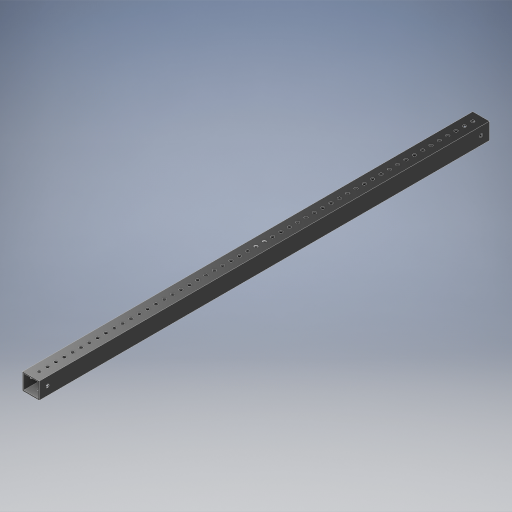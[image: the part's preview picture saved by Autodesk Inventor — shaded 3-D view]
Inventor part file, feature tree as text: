
AUTODESK INVENTOR PART (.ipt)
format: ipt  version: 2024.2 (Build 282272000, 272)  size: 855,040 bytes
history: native  units: in
note: dims shown in document units (in); Inventor stores cm internally (conversion verified against a paired STEP export)
features: other x13, extrude x9, hole x3, pattern_linear x3, mirror x3, sheet_metal_op x1, plane x1
ambient origin geometry x8: Origin, YZ Plane, XZ Plane, XY Plane, X Axis, Y Axis, Z Axis, Center Point
bodies: Solid1 (feature_tree)
feature tree (33):
  other  "Blocks"
  other  "Base Sketch"
  extrude  "Base"  Depth=1.0in
  extrude  "MAX Corner"  Depth=1.0in
  extrude  "MAX Corner Cut"  Depth=0.0625in
  extrude  "Scribe Lines"  Depth=0.0625in
  other  "Side Middle"
  other  "Top Middle"
  other  "Side Holes Sketch"
  hole  "Top Side Hole"  [1 undecoded]
  hole  "Mid Side Hole"  [1 undecoded]
  hole  "Btm Side Hole"  [1 undecoded]
  pattern_linear  "Side Holes"  Spacing1=0.04in  [1 undecoded]
  mirror  "Side Mirror"
  extrude  "MAXTube Hole"  Depth=0.04in
  extrude  "MAXTube Outside"  Depth=27.0in
  pattern_linear  "MAXTube Pattern"  Spacing1=0.0in  [1 undecoded]
  mirror  "MAXTube Mirror"
  extrude  "Left Top Hole"  Depth=27.0in
  extrude  "Mid Top Hole"  TaperAngle=0.0deg  [1 undecoded]
  extrude  "Right Top Hole"  TaperAngle=0.0deg  [1 undecoded]
  pattern_linear  "Top Holes"  Spacing1=0.005in  [1 undecoded]
  mirror  "Top Mirror"
  sheet_metal_op  "Corner"
  other  "MAXTube"
  plane  "Work Plane3"
  other  "Corner:5"
  other  "Corner:6"
  other  "Corner:7"
  other  "Corner:8"
  other  "MAXTube:1"
  other  "MAXTube:2"
  other  "MAXTube:3"
note: 8 required parameter values undecoded (feature->parameter linkage not recoverable at this tier; creation-order binding heuristic only, values carry confidence <= 0.55)
